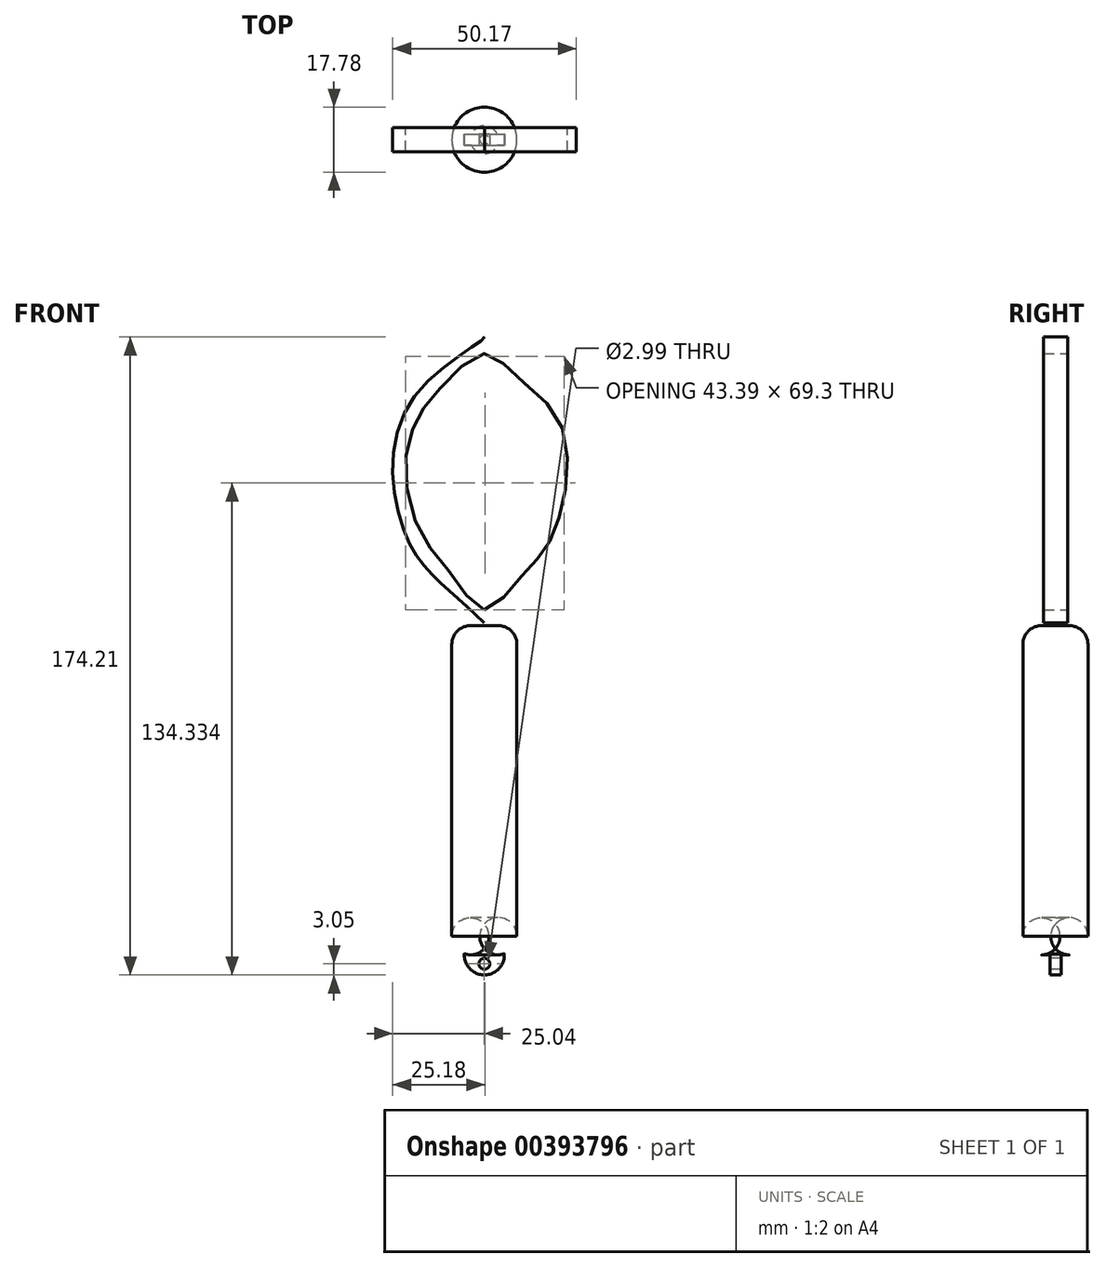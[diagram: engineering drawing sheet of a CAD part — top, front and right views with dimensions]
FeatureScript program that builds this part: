
annotation { "Feature Type Name" : "Feature", "Feature Type Description" : "" }
export const myFeature = defineFeature(function(context is Context, id is Id, definition is map)
    precondition{}
    {
        {
            var Q0;
            Q0=qCreatedBy(makeId("Top.planeOp"),FACE);
            var sketch = newSketch(context, id + "F0", { "sketchPlane" : qUnion([Q0])});
            skCircle(sketch, "E0", {"center": v(0, 0) * mm, "radius": 8.9 * mm});
            skSolve(sketch);
        }
        {
            var Q0;
            Q0=makeQuery(id+"F0.imprint","IMPRINT",FACE,{"disambiguationData":[TD([[makeQuery(id+"F0.imprint","IMPRINT",EDGE,{"derivedFrom":sQuery(id+"F0.wireOp",EDGE,"E0")}),1.0]])]});
            extrude(context, id + "F1", {"entities" : qUnion([Q0]), "depth" : 89.92 * mm});
        }
        {
            var Q0;
            Q0=qCreatedBy(makeId("Front.planeOp"),FACE);
            var sketch = newSketch(context, id + "F2", { "sketchPlane" : qUnion([Q0])});
            skArc(sketch, "E1", {"start": v(-5.42, 0.74) * mm, "mid": v(0.26, -5.46) * mm, "end": v(5.32, 1.25) * mm});
            skLineSegment(sketch, "E2", {"start": v(-5.42, 0.74) * mm, "end": v(5.32, 1.25) * mm});
            skSolve(sketch);
        }
        {
            var Q0;
            Q0=makeQuery(id+"F2.imprint","IMPRINT",FACE,{"disambiguationData":[TD([[makeQuery(id+"F2.imprint","IMPRINT",EDGE,{"derivedFrom":sQuery(id+"F2.wireOp",EDGE,"E1")}),1.0]])]});
            extrude(context, id + "F3", {"entities" : qUnion([Q0]), "operationType" : NewBodyOperationType.ADD, "endBound" : BoundingType.SYMMETRIC, "oppositeDirection" : true, "depth" : 3.05 * mm});
        }
        {
            var Q0;
            Q0=makeQuery(id+"F3.opExtrude","CAP_FACE",FACE,{"disambiguationData":[OSD([sQuery(id+"F2.wireOp",EDGE,"E1"),sQuery(id+"F2.wireOp",EDGE,"E2")])],"isStart":true});
            var sketch = newSketch(context, id + "F4", { "sketchPlane" : qUnion([Q0])});
            skCircle(sketch, "E3", {"center": v(0, -2.42) * mm, "radius": 1.5 * mm});
            skPoint(sketch, "E3.centerSnap0", {"position": v(0, -5.47) * mm});
            skSolve(sketch);
        }
        {
            var Q0;
            Q0=makeQuery(id+"F4.imprint","IMPRINT",FACE,{"disambiguationData":[TD([[makeQuery(id+"F4.imprint","IMPRINT",EDGE,{"derivedFrom":sQuery(id+"F4.wireOp",EDGE,"E3")}),1.0]])]});
            var Q1;
            Q1=sQuery(id+"F4.wireOp",EDGE,"E3");
            extrude(context, id + "F5", {"entities" : qUnion([Q0]), "operationType" : NewBodyOperationType.REMOVE, "surfaceEntities" : qUnion([Q1]), "endBound" : BoundingType.THROUGH_ALL, "oppositeDirection" : true, "depth" : 25.4 * mm});
        }
        {
            var Q0;
            Q0=qCreatedBy(makeId("Front.planeOp"),FACE);
            var sketch = newSketch(context, id + "F6", { "sketchPlane" : qUnion([Q0])});
            skFitSpline(sketch, "E4", {"points": [v(0, 90.74) * mm, v(-10.85, 100.6) * mm, v(-21.26, 114.09) * mm, v(-20.32, 150.79) * mm, v(0, 168.55) * mm, v(0, 169.14) * mm], "startDerivative": vector(-57, 51.55) * mm, "endDerivative": vector(-6.69, 12.69) * mm});
            skLineSegment(sketch, "E5", {"start": v(0.09, 168.98) * mm, "end": v(0, 90.74) * mm, "construction": true});
            skFitSpline(sketch, "E6.MirrorCS", {"points": [v(0, 90.74) * mm, v(10.87, 100.58) * mm, v(21.3, 114.04) * mm, v(20.45, 150.74) * mm, v(0.17, 168.55) * mm, v(0.17, 169.14) * mm], "startDerivative": vector(57.1, 51.43) * mm, "endDerivative": vector(6.72, 12.67) * mm});
            skSolve(sketch);
        }
        {
            var Q0;
            {var subQ0=sQuery(id+"F6.wireOp",EDGE,"E6.MirrorCS");var subQ1=sQuery(id+"F6.wireOp",EDGE,"E4");var subQ2=makeQuery(id+"F6.imprint","INTERSECT",VERTEX,{"disambiguationData":[OD(0.0)],"derivedFrom":[subQ1,subQ0]});Q0=makeQuery(id+"F6.imprint","IMPRINT",FACE,{"disambiguationData":[TD([[makeQuery(id+"F6.imprint","IMPRINT",EDGE,{"disambiguationData":[TD([[subQ2,-1.0]])],"derivedFrom":subQ1}),-1.0]])]});}
            var Q1;
            Q1=sQuery(id+"F6.wireOp",EDGE,"E6.MirrorCS");
            var Q2;
            Q2=sQuery(id+"F6.wireOp",EDGE,"E4");
            extrude(context, id + "F7", {"entities" : qUnion([Q0]), "surfaceEntities" : qUnion([Q1, Q2]), "endBound" : BoundingType.SYMMETRIC, "depth" : 6.6 * mm});
        }
        {
            var Q0;
            Q0=makeQuery(id+"F7.opExtrude","CAP_FACE",FACE,{"disambiguationData":[OSD([sQuery(id+"F6.wireOp",EDGE,"E4"),sQuery(id+"F6.wireOp",EDGE,"E6.MirrorCS")])],"isStart":false});
            var sketch = newSketch(context, id + "F8", { "sketchPlane" : qUnion([Q0])});
            skFitSpline(sketch, "E7", {"points": [v(0, 94.21) * mm, v(8.57, 101.62) * mm, v(15.06, 108.83) * mm, v(19.64, 116.97) * mm, v(22.64, 132.44) * mm, v(19.5, 147.66) * mm, v(7.8, 158.84) * mm, v(0, 164.23) * mm, v(-11.3, 155.61) * mm, v(-18.14, 146.75) * mm, v(-21.55, 134.37) * mm, v(-17.48, 115.47) * mm, v(-8.35, 103.02) * mm, v(0, 94.21) * mm]});
            skSolve(sketch);
        }
        {
            var Q0;
            Q0 = qSketchRegion(id + "F8", true);
            extrude(context, id + "F9", {"entities" : qUnion([Q0]), "operationType" : NewBodyOperationType.REMOVE, "endBound" : BoundingType.THROUGH_ALL, "oppositeDirection" : true, "depth" : 25.4 * mm});
        }
        {
            var Q0;
            Q0=makeQuery(id+"F1.opExtrude","SWEPT_FACE",FACE,{"disambiguationData":[OSD([sQuery(id+"F0.wireOp",EDGE,"E0")])]});
            fillet(context, id + "F10", {"entities" : qUnion([Q0]), "radius" : 5.08 * mm, "tangentPropagation" : true, "allowEdgeOverflow" : false});
        }
    });
